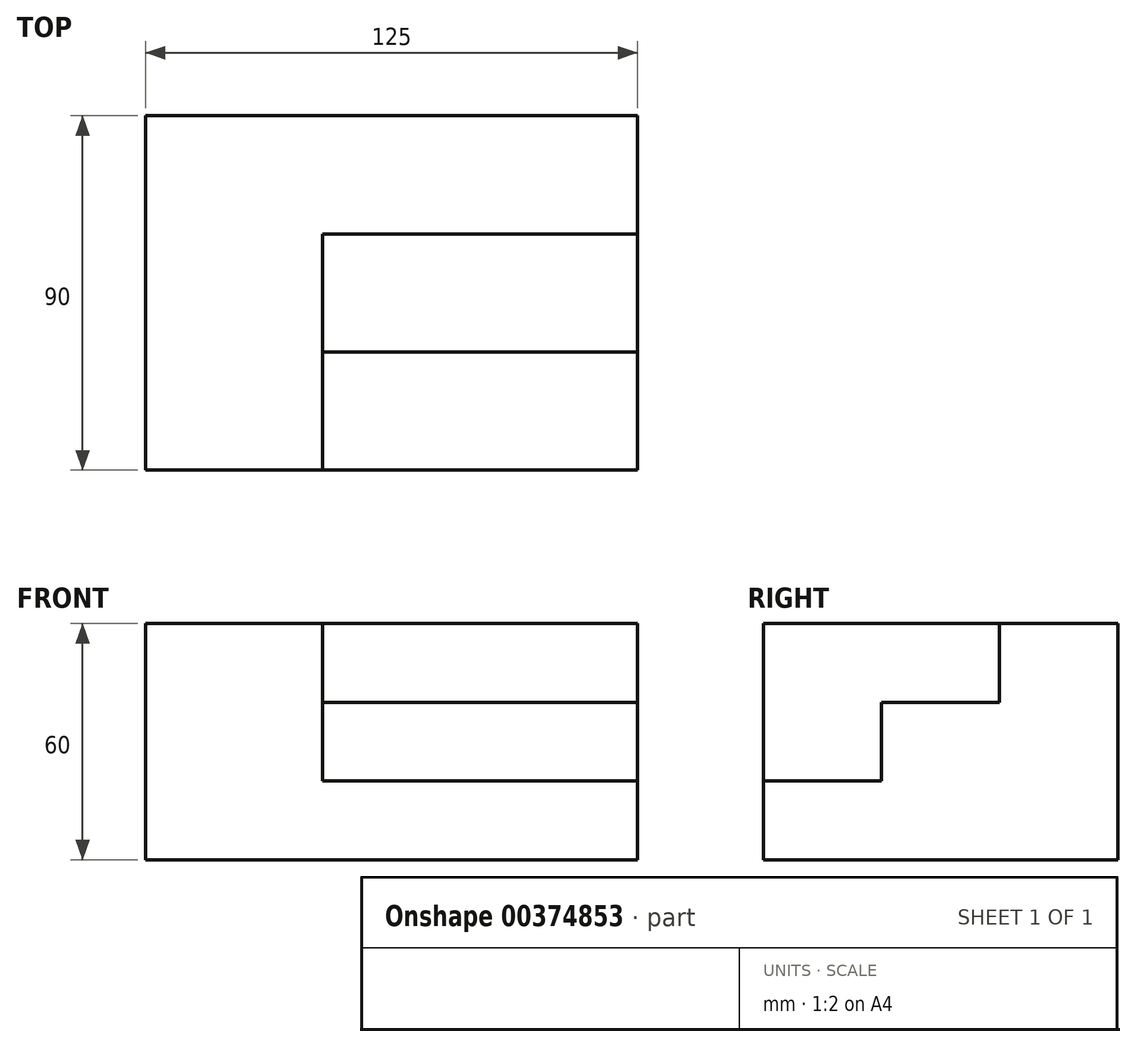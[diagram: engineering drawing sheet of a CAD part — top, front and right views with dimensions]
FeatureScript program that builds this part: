
annotation { "Feature Type Name" : "Feature", "Feature Type Description" : "" }
export const myFeature = defineFeature(function(context is Context, id is Id, definition is map)
    precondition{}
    {
        {
            var Q0;
            Q0=qCreatedBy(makeId("Top.planeOp"),FACE);
            var sketch = newSketch(context, id + "F0", { "sketchPlane" : qUnion([Q0])});
            skLineSegment(sketch, "E0.bottom", {"start": v(-82.4, -32.25) * mm, "end": v(42.6, -32.25) * mm});
            skLineSegment(sketch, "E0.top", {"start": v(-82.4, -122.25) * mm, "end": v(42.6, -122.25) * mm});
            skLineSegment(sketch, "E0.left", {"start": v(-82.4, -32.25) * mm, "end": v(-82.4, -122.25) * mm});
            skLineSegment(sketch, "E0.right", {"start": v(42.6, -32.25) * mm, "end": v(42.6, -122.25) * mm});
            skSolve(sketch);
        }
        {
            var Q0;
            Q0=makeQuery(id+"F0.imprint","IMPRINT",FACE,{"disambiguationData":[TD([[makeQuery(id+"F0.imprint","IMPRINT",EDGE,{"derivedFrom":sQuery(id+"F0.wireOp",EDGE,"E0.bottom")}),-1.0]])]});
            extrude(context, id + "F1", {"entities" : qUnion([Q0]), "depth" : 60 * mm});
        }
        {
            var Q0;
            Q0=makeQuery(id+"F1.opExtrude","SWEPT_FACE",FACE,{"disambiguationData":[OSD([sQuery(id+"F0.wireOp",EDGE,"E0.right")])]});
            var sketch = newSketch(context, id + "F2", { "sketchPlane" : qUnion([Q0])});
            skLineSegment(sketch, "E1", {"start": v(-122.25, 0) * mm, "end": v(-122.25, 20) * mm});
            skLineSegment(sketch, "E2", {"start": v(-122.25, 20) * mm, "end": v(-92.25, 20) * mm});
            skLineSegment(sketch, "E3", {"start": v(-92.25, 20) * mm, "end": v(-92.25, 40) * mm});
            skLineSegment(sketch, "E4", {"start": v(-92.25, 40) * mm, "end": v(-62.25, 40) * mm});
            skLineSegment(sketch, "E5", {"start": v(-62.25, 40) * mm, "end": v(-62.25, 60) * mm});
            skLineSegment(sketch, "E6", {"start": v(-62.25, 60) * mm, "end": v(-5.93, 60) * mm});
            skLineSegment(sketch, "E7", {"start": v(-5.93, 60) * mm, "end": v(-5.93, 87.13) * mm});
            skLineSegment(sketch, "E8", {"start": v(-5.93, 87.13) * mm, "end": v(-175.8, 87.13) * mm});
            skLineSegment(sketch, "E9", {"start": v(-175.8, 87.13) * mm, "end": v(-122.25, 20) * mm});
            skSolve(sketch);
        }
        {
            var Q0;
            {var subQ5=sQuery(id+"F2.wireOp",EDGE,"E2");Q0=makeQuery(id+"F2.imprint","IMPRINT",FACE,{"disambiguationData":[TD([[makeQuery(id+"F2.imprint","IMPRINT",EDGE,{"derivedFrom":subQ5}),1.0]])]});}
            extrude(context, id + "F3", {"entities" : qUnion([Q0]), "operationType" : NewBodyOperationType.REMOVE, "oppositeDirection" : true, "depth" : 80 * mm});
        }
    });
